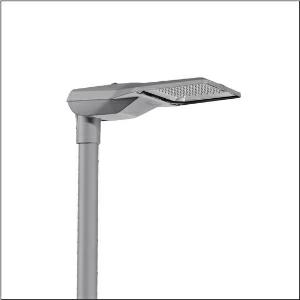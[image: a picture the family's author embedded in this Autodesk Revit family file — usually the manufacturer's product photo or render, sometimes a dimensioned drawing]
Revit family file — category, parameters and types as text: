
# Revit family: streetlight_sl_21_midi___st1_0ab_5xe3m33s08mb_fd22
name_source: partatom
category: Lighting Fixtures
units: mm (PartAtom-declared; Revit-internal decimal feet)

## family parameters
Cut with Voids When Loaded = No
Host = Face
Light Source = No
Part Type = Normal
Room Calculation Point = No
Round Connector Dimension = Use Diameter
Shared = No

## types (1)
- --- (1 x LED, 16080 lm, 136 W, 3000K)
    Apparent Load = 136 VA
    CIE Flux Codes = 38 73 97 100 100
    Color Rendering = 70
    Color Temperature = 3000K
    Default Elevation = 1800 mm
    Description = Streetlight SL 21 midi, mast luminaire, primary light control with lens, of PMMA, primary optical cover: cover, of toughened safety glass, transparent, light distribution: ST1.0aB, light emission: direct distribution, primary light characteristic: asymmetric, installation type: side-entry, post-top, LED, High Power LED, rated luminous flux: 16.080lm, luminous efficacy: 118lm/W, light colour: 730, colour temperature: 3000K, control: flexible luminous flux parameterisation, time-dependent luminous flux control, constant luminous flux control, overheat protection, presetting dimming logarithmic, mains connection: 230..240V, AC, 50/60Hz, start of lifetime: 136W, end of service life: 142W, reduction: 61W, luminaire housing, of diecast aluminium, powder-coated, Siteco® metallic grey (DB 702S), corrosivity category C5 mid according to DIN EN ISO 12944, please order mast flange separately, inclination adjustable: 0°, 5°, 10°, 15°, sealing non-destructively replaceable, multi-level sealing system, length: 644mm, width: 335mm, height: 110mm, mast flange for spigot size: 42mm (side-entry): 5XC10008XM4, 60/48mm (side-entry/post-top): 5XC10108XM2, 76/60mm (side-entry/post-top): 5XC10108XM1, Smart Interface above, protection rating (complete): IP66, insulation class (complete): insulation class II (safety insulation), certification: CE, ENEC, ENEC+, VDE, impact resistance: IK09, permissible operating ambient temperature for outdoor applications: -40..+50°C, standard-compliant lighting for roads and squares, packaging unit: 1 piece

Light Distribution: ST1.0aB
    Height = 111 mm
    Lamp = 1 x LED
    Lamp Light Flux = 16080 lm
    Lamp Power = 136 W
    Lamp count = 1
    Length = 644 mm
    Luminous efficacy = 118 lm/W
    Manufacturer = Siteco
    ModVariant = No
    Model = 5XE3M33S08MB
    Number of Poles = 1
    OnlyDefault = Yes
    Power Factor = 1
    Product Name = Streetlight SL 21 midi | ST1.0aB
    Product group = mast luminaire | pylon top
    ProductGroupID = 6100
    Protection Class = Protection class II
    Protection Degree = IP 66
    RLX_Detail_Level = 1
    RLX_Emergency_Light_Flux = 0 lm
    RLX_Emergency_Type = 0
    RLX_Emergency_Type_DB = No
    RlxData = <blob elided: 90417 chars, md5=c0fa6604>
    Socket = socket
    Standby Power = 0 W
    System Light Flux = 16081 lm
    System Power = 136 W
    Type Comments = factory setting: luminous flux: 100 % | dim-lin: 254 | 695 mA
    Type Image = l_1004302.jpg
    URL = http://relux.com
    VarID = @adj_134405
    Voltage = 0 V
    Weight = 0.00 kg
    Width = 336 mm

## geometry (parser evidence)
native form markers: Blend x4, Sweep x10
no freeform markers — native parametric forms only
